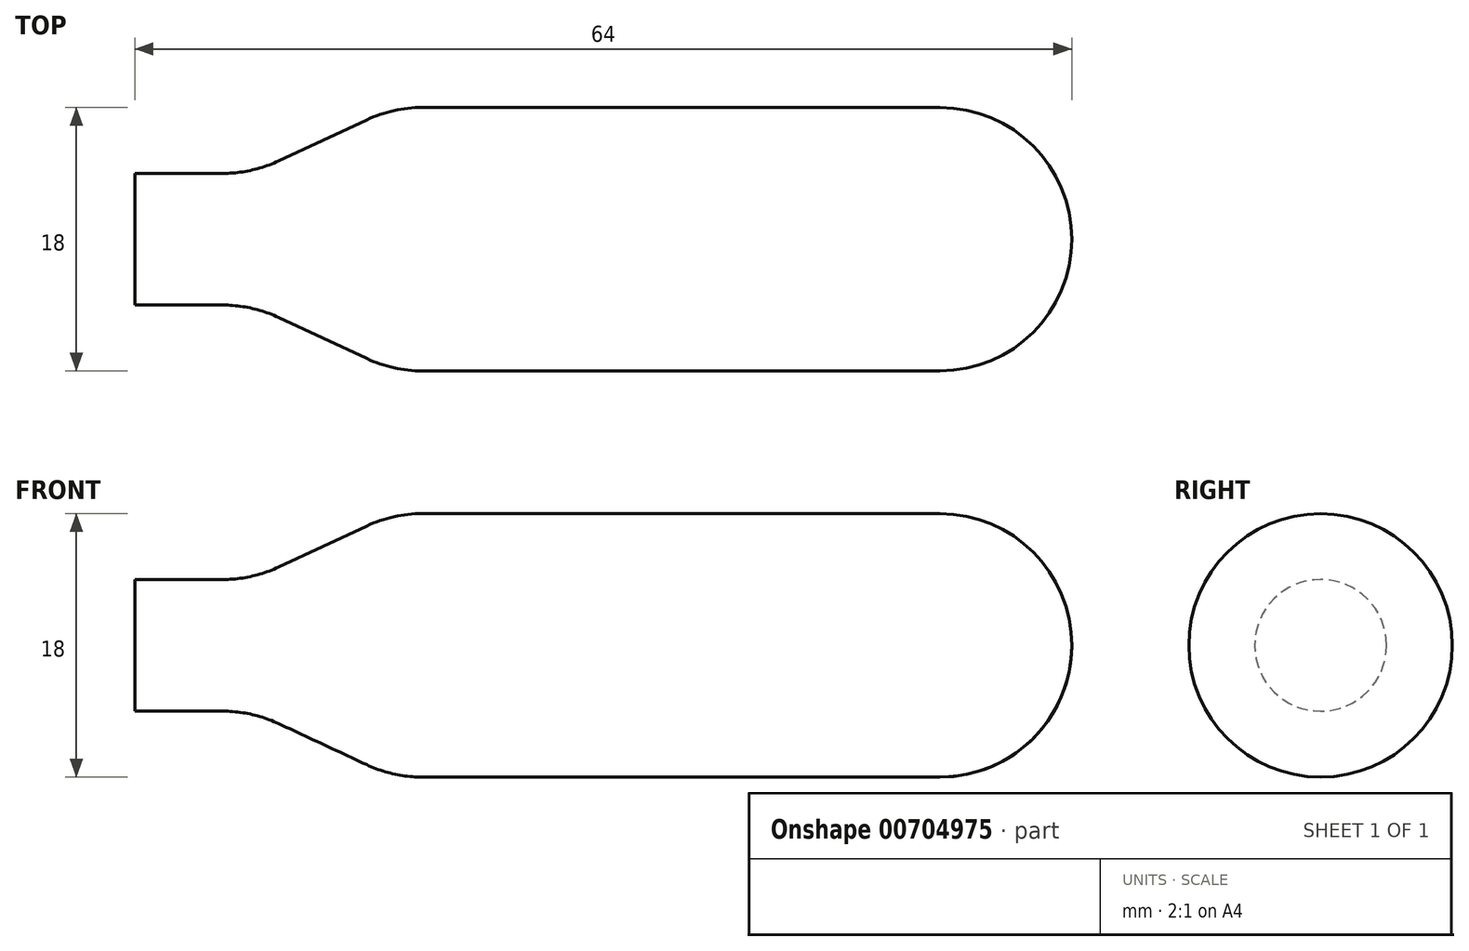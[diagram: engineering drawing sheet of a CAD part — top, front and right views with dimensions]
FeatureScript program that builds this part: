
annotation { "Feature Type Name" : "Feature", "Feature Type Description" : "" }
export const myFeature = defineFeature(function(context is Context, id is Id, definition is map)
    precondition{}
    {
        {
            var Q0;
            Q0=qCreatedBy(makeId("Front.planeOp"),FACE);
            var sketch = newSketch(context, id + "F0", { "sketchPlane" : qUnion([Q0])});
            skLineSegment(sketch, "E0", {"start": v(0, 0) * mm, "end": v(0, 4.5) * mm});
            skLineSegment(sketch, "E1", {"start": v(0, 4.5) * mm, "end": v(6, 4.5) * mm});
            skLineSegment(sketch, "E2", {"start": v(19.64, 9) * mm, "end": v(55, 9) * mm});
            skLineSegment(sketch, "E3", {"start": v(64, 0) * mm, "end": v(64, 0) * mm});
            skLineSegment(sketch, "E4", {"start": v(64, 0) * mm, "end": v(0, 0) * mm});
            skLineSegment(sketch, "E5", {"start": v(9.8, 5.34) * mm, "end": v(15.83, 8.16) * mm});
            skPoint(sketch, "E6.visualSharp", {"position": v(64, 9) * mm});
            skArc(sketch, "E6.filletArc", {"start": v(64, 0) * mm, "mid": v(61.36, 6.36) * mm, "end": v(55, 9) * mm});
            skPoint(sketch, "E7.visualSharp", {"position": v(17.64, 9) * mm});
            skArc(sketch, "E7.filletArc", {"start": v(19.64, 9) * mm, "mid": v(17.7, 8.79) * mm, "end": v(15.83, 8.16) * mm});
            skPoint(sketch, "E8.visualSharp", {"position": v(8, 4.5) * mm});
            skArc(sketch, "E8.filletArc", {"start": v(6, 4.5) * mm, "mid": v(7.95, 4.71) * mm, "end": v(9.8, 5.34) * mm});
            skSolve(sketch);
        }
        {
            var Q0;
            Q0=makeQuery(id+"F0.imprint","IMPRINT",FACE,{"disambiguationData":[TD([[makeQuery(id+"F0.imprint","IMPRINT",EDGE,{"derivedFrom":sQuery(id+"F0.wireOp",EDGE,"E0")}),-1.0]])]});
            var Q1;
            Q1=sQuery(id+"F0.wireOp",EDGE,"E4");
            revolve(context, id + "F1", {"surfaceOperationType" : NewSurfaceOperationType.NEW, "entities" : qUnion([Q0]), "axis" : qUnion([Q1]), "revolveType" : RevolveType.FULL});
        }
    });
